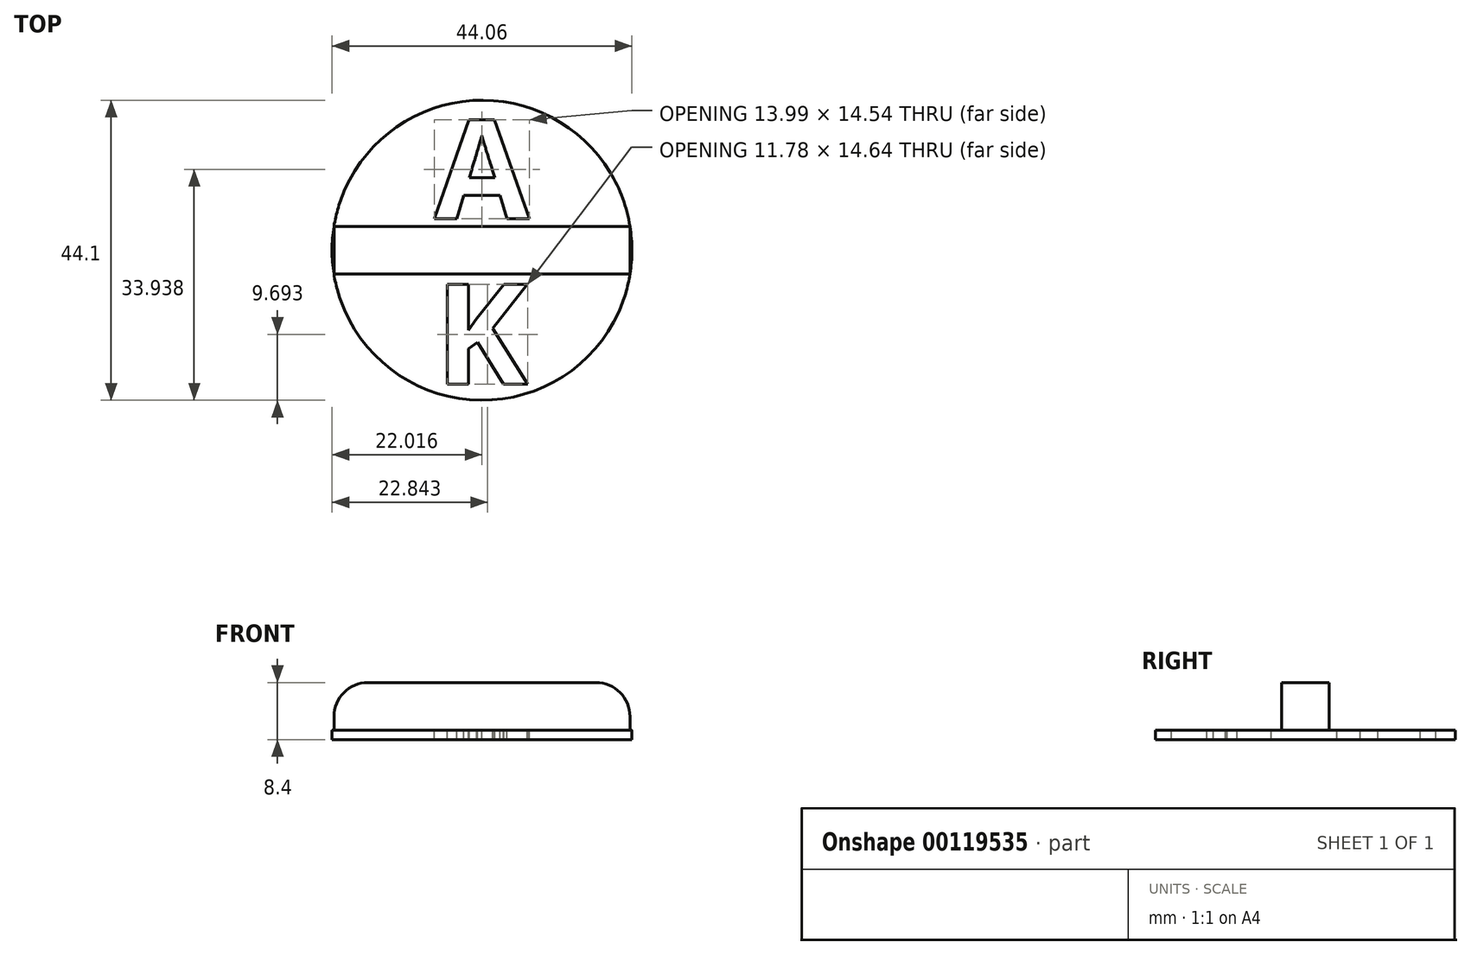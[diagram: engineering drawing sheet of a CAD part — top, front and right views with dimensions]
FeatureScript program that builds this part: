
annotation { "Feature Type Name" : "Feature", "Feature Type Description" : "" }
export const myFeature = defineFeature(function(context is Context, id is Id, definition is map)
    precondition{}
    {
        {
            var Q0;
            Q0=qCreatedBy(makeId("Top.planeOp"),FACE);
            var sketch = newSketch(context, id + "F0", { "sketchPlane" : qUnion([Q0])});
            skCircle(sketch, "E0", {"center": v(0, 0) * mm, "radius": 22.05 * mm});
            skSolve(sketch);
        }
        {
            var Q0;
            Q0 = qSketchRegion(id + "F0", true);
            extrude(context, id + "F1", {"entities" : qUnion([Q0]), "depth" : 1.4 * mm});
        }
        {
            var Q0;
            Q0=makeQuery(id+"F1.opExtrude","CAP_FACE",FACE,{"disambiguationData":[OSD([sQuery(id+"F0.wireOp",EDGE,"E0")])],"isStart":false});
            var sketch = newSketch(context, id + "F2", { "sketchPlane" : qUnion([Q0])});
            skLineSegment(sketch, "E1.bottom", {"start": v(-22.75, 3.5) * mm, "end": v(24.13, 3.5) * mm});
            skLineSegment(sketch, "E1.top", {"start": v(-22.75, -3.5) * mm, "end": v(24.13, -3.5) * mm});
            skLineSegment(sketch, "E1.left", {"start": v(-22.75, 3.5) * mm, "end": v(-22.75, -3.5) * mm});
            skLineSegment(sketch, "E1.right", {"start": v(24.13, 3.5) * mm, "end": v(24.13, -3.5) * mm});
            skSolve(sketch);
        }
        {
            var Q0;
            Q0 = qSketchRegion(id + "F2", true);
            extrude(context, id + "F3", {"entities" : qUnion([Q0]), "operationType" : NewBodyOperationType.ADD, "depth" : 7 * mm});
        }
        {
            var Q0;
            Q0=makeQuery(id+"F3.opExtrude","CAP_FACE",FACE,{"disambiguationData":[OSD([sQuery(id+"F2.wireOp",EDGE,"E1.bottom"),sQuery(id+"F2.wireOp",EDGE,"E1.top"),sQuery(id+"F2.wireOp",EDGE,"E1.left"),sQuery(id+"F2.wireOp",EDGE,"E1.right")])],"isStart":false});
            var sketch = newSketch(context, id + "F4", { "sketchPlane" : qUnion([Q0])});
            skLineSegment(sketch, "E2", {"start": v(-20.13, 9) * mm, "end": v(-25.9, 9.52) * mm});
            skLineSegment(sketch, "E3", {"start": v(-25.9, 9.52) * mm, "end": v(-31.14, -2.83) * mm});
            skLineSegment(sketch, "E4", {"start": v(-31.14, -2.83) * mm, "end": v(-22.4, -9.36) * mm});
            skLineSegment(sketch, "E5", {"start": v(-22.4, -9.36) * mm, "end": v(-20.22, -8.78) * mm});
            skLineSegment(sketch, "E6", {"start": v(18.85, 11.44) * mm, "end": v(25.7, 10.69) * mm});
            skLineSegment(sketch, "E7", {"start": v(25.7, 10.69) * mm, "end": v(31.01, 2.28) * mm});
            skLineSegment(sketch, "E8", {"start": v(31.01, 2.28) * mm, "end": v(27.39, -8.07) * mm});
            skLineSegment(sketch, "E9", {"start": v(27.39, -8.07) * mm, "end": v(20.08, -9.1) * mm});
            skArc(sketch, "E10", {"start": v(20.08, -9.1) * mm, "mid": v(21.98, 1.32) * mm, "end": v(18.85, 11.44) * mm});
            skArc(sketch, "E11", {"start": v(-20.13, 9) * mm, "mid": v(-22.04, 0.12) * mm, "end": v(-20.22, -8.78) * mm});
            skSolve(sketch);
        }
        {
            var Q0;
            Q0 = qSketchRegion(id + "F4", true);
            extrude(context, id + "F5", {"entities" : qUnion([Q0]), "operationType" : NewBodyOperationType.REMOVE, "oppositeDirection" : true, "depth" : 25 * mm});
        }
        {
            var Q0;
            Q0=makeQuery(id+"F3.opExtrude","SWEPT_FACE",FACE,{"disambiguationData":[OSD([sQuery(id+"F2.wireOp",EDGE,"E1.top")])]});
            var sketch = newSketch(context, id + "F6", { "sketchPlane" : qUnion([Q0])});
            skLineSegment(sketch, "E12.left", {"start": v(-21.77, 3.4) * mm, "end": v(-21.77, 1.4) * mm});
            skLineSegment(sketch, "E12.right", {"start": v(21.75, 3.4) * mm, "end": v(21.75, 1.4) * mm});
            skPoint(sketch, "E13.visualSharp", {"position": v(-21.77, 8.4) * mm});
            skArc(sketch, "E13.filletArc", {"start": v(-16.77, 8.4) * mm, "mid": v(-20.3, 6.94) * mm, "end": v(-21.77, 3.4) * mm});
            skPoint(sketch, "E14.visualSharp", {"position": v(21.75, 8.4) * mm});
            skArc(sketch, "E14.filletArc", {"start": v(21.75, 3.4) * mm, "mid": v(20.28, 6.94) * mm, "end": v(16.75, 8.4) * mm});
            skLineSegment(sketch, "E15", {"start": v(-21.77, 1.4) * mm, "end": v(-25.3, 1.4) * mm});
            skLineSegment(sketch, "E16", {"start": v(-25.3, 1.4) * mm, "end": v(-23.92, 13.16) * mm});
            skLineSegment(sketch, "E17", {"start": v(-23.92, 13.16) * mm, "end": v(-18.42, 12.5) * mm});
            skLineSegment(sketch, "E18", {"start": v(-18.42, 12.5) * mm, "end": v(-16.77, 8.4) * mm});
            skLineSegment(sketch, "E19", {"start": v(16.75, 8.4) * mm, "end": v(17.95, 11.69) * mm});
            skLineSegment(sketch, "E20", {"start": v(17.95, 11.69) * mm, "end": v(26.36, 8.67) * mm});
            skLineSegment(sketch, "E21", {"start": v(26.36, 8.67) * mm, "end": v(25.54, 1.89) * mm});
            skLineSegment(sketch, "E22", {"start": v(21.75, 1.4) * mm, "end": v(24.03, 1.4) * mm});
            skLineSegment(sketch, "E23", {"start": v(24.03, 1.4) * mm, "end": v(25.54, 1.89) * mm});
            skSolve(sketch);
        }
        {
            var Q0;
            Q0 = qSketchRegion(id + "F6", true);
            extrude(context, id + "F7", {"entities" : qUnion([Q0]), "operationType" : NewBodyOperationType.REMOVE, "oppositeDirection" : true, "depth" : 25 * mm});
        }
        {
            var Q0;
            {var subQ0=sQuery(id+"F0.wireOp",EDGE,"E0");var subQ1=sQuery(id+"F2.wireOp",EDGE,"E1.bottom");Q0=makeQuery(id+"F3.boolean.opBoolean","SPLIT",FACE,{"disambiguationData":[TD([makeQuery(id+"F3.opExtrude","SWEPT_FACE",FACE,{"disambiguationData":[OSD([subQ1])]})])],"derivedFrom":makeQuery(id+"F1.opExtrude","CAP_FACE",FACE,{"disambiguationData":[OSD([subQ0])],"isStart":false})});}
            var sketch = newSketch(context, id + "F8", { "sketchPlane" : qUnion([Q0])});
            skText(sketch, "E24", { "text": "A", "fontName": "OpenSans-Bold.ttf"});
            const initialGuessF8  = {"E24": [-0.00702, 0.00462, 1, 0, 0.0146]};
            skSetInitialGuess(sketch, initialGuessF8);
            skSolve(sketch);
        }
        {
            var Q0;
            Q0 = qSketchRegion(id + "F8", true);
            var Q1;
            Q1 = qConstructionFilter(qBodyType(qCreatedBy(id + "F8" ,EDGE), BodyType.WIRE), ConstructionObject.NO);
            extrude(context, id + "F9", {"entities" : qUnion([Q0]), "operationType" : NewBodyOperationType.REMOVE, "surfaceEntities" : qUnion([Q1]), "oppositeDirection" : true, "depth" : 5 * mm});
        }
        {
            var Q0;
            {var subQ0=sQuery(id+"F0.wireOp",EDGE,"E0");var subQ1=sQuery(id+"F2.wireOp",EDGE,"E1.top");Q0=makeQuery(id+"F3.boolean.opBoolean","SPLIT",FACE,{"disambiguationData":[TD([makeQuery(id+"F3.opExtrude","SWEPT_FACE",FACE,{"disambiguationData":[OSD([subQ1])]})])],"derivedFrom":makeQuery(id+"F1.opExtrude","CAP_FACE",FACE,{"disambiguationData":[OSD([subQ0])],"isStart":false})});}
            var sketch = newSketch(context, id + "F10", { "sketchPlane" : qUnion([Q0])});
            skText(sketch, "E25", { "text": "K", "fontName": "OpenSans-Bold.ttf"});
            const initialGuessF10  = {"E25": [-0.00693, -0.01968, 1, 0, 0.01477]};
            skSetInitialGuess(sketch, initialGuessF10);
            skSolve(sketch);
        }
        {
            var Q0;
            Q0 = qSketchRegion(id + "F10", true);
            var Q1;
            Q1 = qConstructionFilter(qBodyType(qCreatedBy(id + "F10" ,EDGE), BodyType.WIRE), ConstructionObject.NO);
            extrude(context, id + "F11", {"entities" : qUnion([Q0]), "operationType" : NewBodyOperationType.REMOVE, "surfaceEntities" : qUnion([Q1]), "oppositeDirection" : true, "depth" : 5 * mm});
        }
    });
